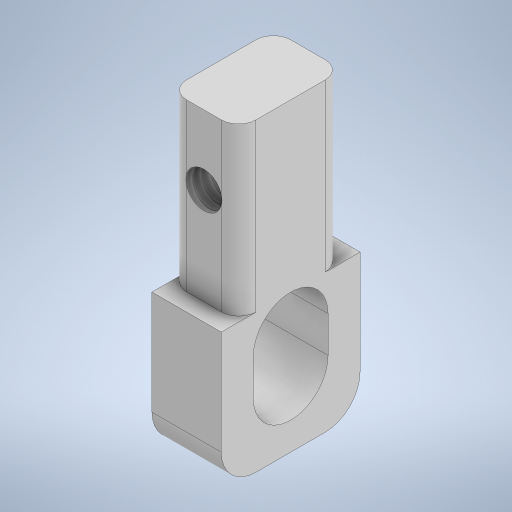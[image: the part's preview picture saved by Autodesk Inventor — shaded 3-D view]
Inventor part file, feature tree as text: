
AUTODESK INVENTOR PART (.ipt)
format: ipt  version: 2023 (Build 270158000, 158)  size: 311,808 bytes
history: native  units: in
note: dims shown in document units (in); Inventor stores cm internally (conversion verified against a paired STEP export)
features: sketch x5, extrude x4, fillet x3, hole x1
ambient origin geometry x8: Origin, YZ Plane, XZ Plane, XY Plane, X Axis, Y Axis, Z Axis, Center Point
bodies: Solid1 (feature_tree)
feature tree (13):
  extrude  "Extrusion1"  Depth=0.25in
  extrude  "Extrusion3"  Depth=0.3in
  extrude  "Extrusion4"  Depth=0.5in
  extrude  "Extrusion5"  Depth=0.0625in
  fillet  "Fillet2"  Radius=0.0625in
  fillet  "Fillet5"  Radius=0.125in
  fillet  "Fillet10"  Radius=0.1in
  hole  "Hole1"  [1 undecoded]
  sketch  "Sketch1"  dims[d0=0.25in d1=0.375in]
  sketch  "Sketch3"  dims[d2=1.1in d3=0.0in d11=0.3in]
  sketch  "Sketch4"  dims[d18=0.0in d19=0.0in d22=0.5in]
  sketch  "Sketch5"  dims[d23=0.0625in d24=0.0in d25=0.5in d26=0.0625in d27=0.0in d29=0.125in d32=0.1in]
  sketch  "Sketch6"  dims[d33=0.4in d34=0.1348in d39=0.1348in d40=0.1348in d41=0.0625in d42=0.25in d43=0.164in d48=0.13in d49=0.38in d50=0.375in d51=0.25in d52=0.5635in d53=0.3in d54=0.8108in]
note: 1 required parameter value undecoded (feature->parameter linkage not recoverable at this tier; creation-order binding heuristic only, values carry confidence <= 0.55)
